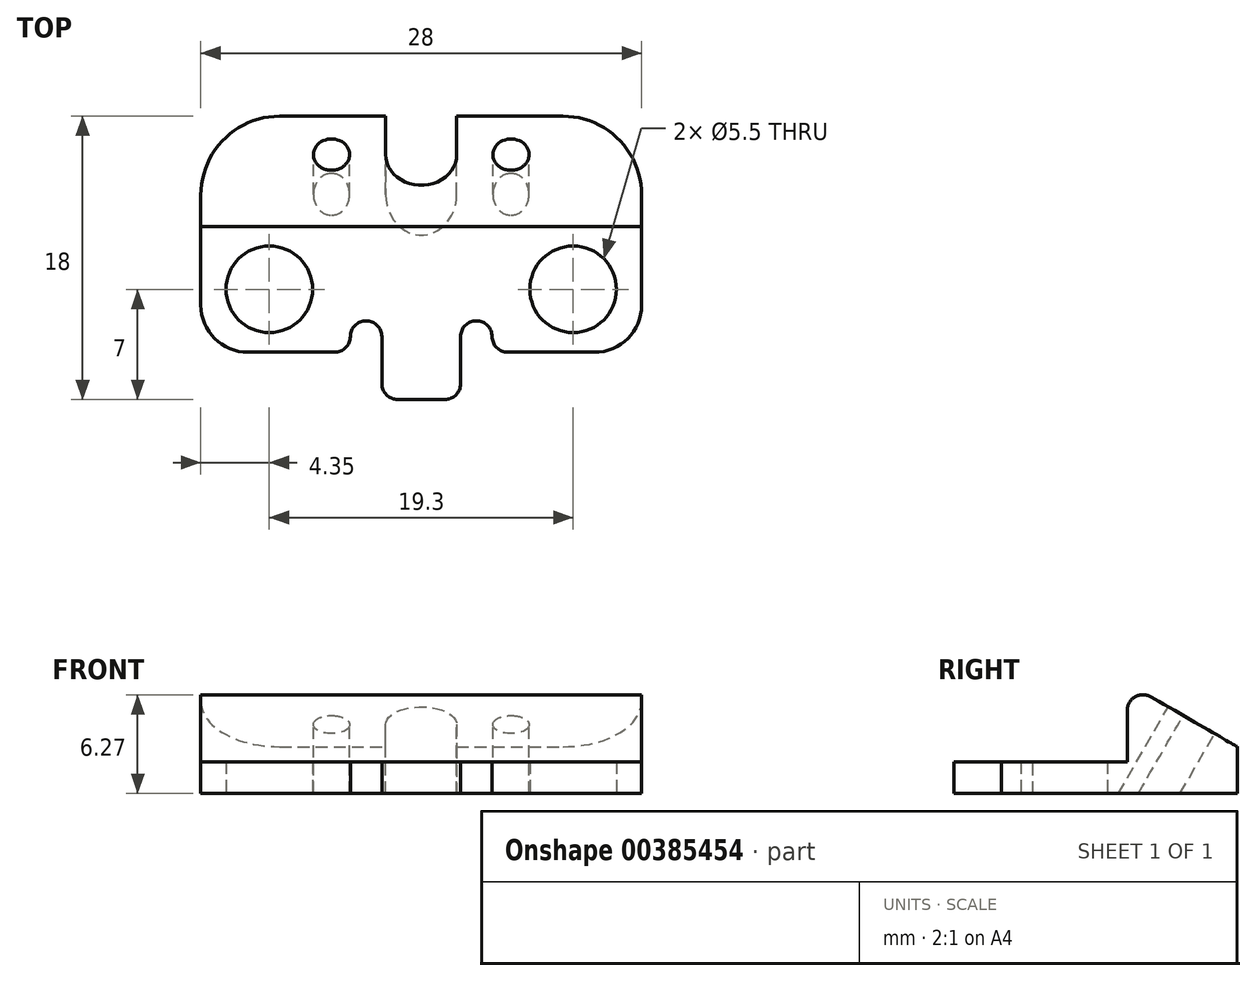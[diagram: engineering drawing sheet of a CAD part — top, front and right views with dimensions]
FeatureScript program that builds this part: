
annotation { "Feature Type Name" : "Feature", "Feature Type Description" : "" }
export const myFeature = defineFeature(function(context is Context, id is Id, definition is map)
    precondition{}
    {
        {
            var Q0;
            Q0=qCreatedBy(makeId("Top.planeOp"),FACE);
            var sketch = newSketch(context, id + "F0", { "sketchPlane" : qUnion([Q0])});
            skLineSegment(sketch, "E0", {"start": v(-14, -10) * mm, "end": v(-14, -2) * mm});
            skLineSegment(sketch, "E1", {"start": v(-14, -2) * mm, "end": v(14, -2) * mm});
            skLineSegment(sketch, "E2", {"start": v(14, -2) * mm, "end": v(14, -10) * mm});
            skLineSegment(sketch, "E3", {"start": v(14, -10) * mm, "end": v(-14, -10) * mm});
            skPoint(sketch, "E4", {"position": v(-9.65, -6) * mm});
            skPoint(sketch, "E4.positionSnap0", {"position": v(-14, -6) * mm});
            skPoint(sketch, "E5", {"position": v(9.65, -6) * mm});
            skPoint(sketch, "E5.positionSnap0", {"position": v(14, -6) * mm});
            skLineSegment(sketch, "E6", {"start": v(-14, -2) * mm, "end": v(-14, 5) * mm});
            skLineSegment(sketch, "E7", {"start": v(-14, 5) * mm, "end": v(14, 5) * mm});
            skLineSegment(sketch, "E8", {"start": v(14, 5) * mm, "end": v(14, -2) * mm});
            skPoint(sketch, "E9", {"position": v(0, 0) * mm});
            skPoint(sketch, "E10.positionSnap0", {"position": v(14, 1.5) * mm});
            skPoint(sketch, "E10.positionSnap1", {"position": v(0, 5) * mm});
            skLineSegment(sketch, "E11", {"start": v(2.5, -10) * mm, "end": v(2.5, -13) * mm});
            skLineSegment(sketch, "E12", {"start": v(2.5, -13) * mm, "end": v(-2.5, -13) * mm});
            skLineSegment(sketch, "E13", {"start": v(-2.5, -13) * mm, "end": v(-2.5, -10) * mm});
            skLineSegment(sketch, "E14", {"start": v(2.5, -10) * mm, "end": v(2.5, -8) * mm});
            skLineSegment(sketch, "E15", {"start": v(2.5, -8) * mm, "end": v(4.5, -8) * mm});
            skLineSegment(sketch, "E16", {"start": v(4.5, -8) * mm, "end": v(4.5, -10) * mm});
            skLineSegment(sketch, "E17", {"start": v(-2.5, -10) * mm, "end": v(-2.5, -8) * mm});
            skLineSegment(sketch, "E18", {"start": v(-2.5, -8) * mm, "end": v(-4.5, -8) * mm});
            skLineSegment(sketch, "E19", {"start": v(-4.5, -8) * mm, "end": v(-4.5, -10) * mm});
            skSolve(sketch);
        }
        {
            var Q0;
            Q0=makeQuery(id+"F0.imprint","IMPRINT",FACE,{"disambiguationData":[TD([[makeQuery(id+"F0.imprint","IMPRINT",EDGE,{"derivedFrom":sQuery(id+"F0.wireOp",EDGE,"E0")}),-1.0]])]});
            var Q1;
            {var subQ0=sQuery(id+"F0.wireOp",EDGE,"E11");Q1=makeQuery(id+"F0.imprint","IMPRINT",FACE,{"disambiguationData":[TD([[makeQuery(id+"F0.imprint","IMPRINT",EDGE,{"derivedFrom":subQ0}),-1.0]])]});}
            extrude(context, id + "F1", {"entities" : qUnion([Q0, Q1]), "depth" : 2 * mm, "offsetDistance" : 25 * mm});
        }
        {
            var Q0;
            Q0=makeQuery(id+"F0.imprint","IMPRINT",FACE,{"disambiguationData":[TD([[makeQuery(id+"F0.imprint","IMPRINT",EDGE,{"derivedFrom":sQuery(id+"F0.wireOp",EDGE,"E1")}),1.0]])]});
            extrude(context, id + "F2", {"entities" : qUnion([Q0]), "operationType" : NewBodyOperationType.ADD, "depth" : 7 * mm, "offsetDistance" : 25 * mm});
        }
        {
            var Q0;
            Q0=sQuery(id+"F0.wireOp",VERTEX,"E4");
            var Q1;
            Q1=sQuery(id+"F0.wireOp",VERTEX,"E5");
            var Q2;
            Q2=makeQuery(id+"F1.opExtrude","SWEPT_BODY",BODY,{"disambiguationData":[OSD([sQuery(id+"F0.wireOp",EDGE,"E0"),sQuery(id+"F0.wireOp",EDGE,"E1"),sQuery(id+"F0.wireOp",EDGE,"E2"),sQuery(id+"F0.wireOp",EDGE,"E3")])]});
            hole(context, id + "F3", {"style" : HoleStyle.SIMPLE, "endStyle" : HoleEndStyle.THROUGH, "oppositeDirection" : true, "holeDiameter" : 5.5 * mm, "isTappedThrough" : true, "tappedDepth" : 12 * mm, "tapClearance" : 3, "locations" : qUnion([Q0, Q1]), "scope" : qUnion([Q2])});
        }
        {
            var Q0;
            Q0=makeQuery(id+"F2.boolean.opBoolean","MERGE",FACE,{"derivedFrom":[makeQuery(id+"F1.opExtrude","SWEPT_FACE",FACE,{"disambiguationData":[OSD([sQuery(id+"F0.wireOp",EDGE,"E2")])]}),makeQuery(id+"F2.opExtrude","SWEPT_FACE",FACE,{"disambiguationData":[OSD([sQuery(id+"F0.wireOp",EDGE,"E8")])]})]});
            var sketch = newSketch(context, id + "F4", { "sketchPlane" : qUnion([Q0])});
            skLineSegment(sketch, "E20", {"start": v(-2, 7) * mm, "end": v(5, 2.96) * mm});
            skSolve(sketch);
        }
        {
            var Q0;
            {var subQ0=sQuery(id+"F4.wireOp",EDGE,"E20");Q0=makeQuery(id+"F4.imprint","IMPRINT",FACE,{"disambiguationData":[TD([[makeQuery(id+"F4.imprint","IMPRINT",EDGE,{"derivedFrom":subQ0}),1.0]])]});}
            extrude(context, id + "F5", {"entities" : qUnion([Q0]), "operationType" : NewBodyOperationType.REMOVE, "endBound" : BoundingType.THROUGH_ALL, "oppositeDirection" : true, "depth" : 25 * mm});
        }
        {
            var Q0;
            Q0=makeQuery(id+"F1.opExtrude","SWEPT_EDGE",EDGE,{"disambiguationData":[OSD([sQuery(id+"F0.wireOp",EDGE,"E0"),sQuery(id+"F0.wireOp",EDGE,"E3")])]});
            var Q1;
            Q1=makeQuery(id+"F1.opExtrude","SWEPT_EDGE",EDGE,{"disambiguationData":[OSD([sQuery(id+"F0.wireOp",EDGE,"E2"),sQuery(id+"F0.wireOp",EDGE,"E3")])]});
            fillet(context, id + "F6", {"entities" : qUnion([Q0, Q1]), "radius" : 3 * mm, "tangentPropagation" : true, "allowEdgeOverflow" : false});
        }
        {
            var Q0;
            Q0=makeQuery(id+"F2.opExtrude","SWEPT_EDGE",EDGE,{"disambiguationData":[OSD([sQuery(id+"F0.wireOp",EDGE,"E7"),sQuery(id+"F0.wireOp",EDGE,"E8")])]});
            var Q1;
            Q1=makeQuery(id+"F2.opExtrude","SWEPT_EDGE",EDGE,{"disambiguationData":[OSD([sQuery(id+"F0.wireOp",EDGE,"E6"),sQuery(id+"F0.wireOp",EDGE,"E7")])]});
            fillet(context, id + "F7", {"entities" : qUnion([Q0, Q1]), "radius" : 5 * mm, "tangentPropagation" : true, "allowEdgeOverflow" : false});
        }
        {
            var Q0;
            Q0=makeQuery(id+"F2.opExtrude","SWEPT_EDGE",EDGE,{"disambiguationData":[OSD([sQuery(id+"F0.wireOp",EDGE,"E7"),sQuery(id+"F0.wireOp",EDGE,"al64L23N-QREo-ytZC-Y57I-qEylZoFodaZA")])]});
            var Q1;
            Q1=makeQuery(id+"F2.opExtrude","SWEPT_EDGE",EDGE,{"disambiguationData":[OSD([sQuery(id+"F0.wireOp",EDGE,"E7"),sQuery(id+"F0.wireOp",EDGE,"A9lWMWF5-5aLG-td5A-o3ft-i0FPsXMzaifF")])]});
            var Q2;
            Q2=makeQuery(id+"F2.opExtrude","CAP_EDGE",EDGE,{"disambiguationData":[OSD([sQuery(id+"F0.wireOp",EDGE,"E1")])],"isStart":false});
            var Q3;
            Q3=makeQuery(id+"F1.opExtrude","SWEPT_EDGE",EDGE,{"disambiguationData":[OSD([sQuery(id+"F0.wireOp",EDGE,"E18"),sQuery(id+"F0.wireOp",EDGE,"E19")])]});
            var Q4;
            Q4=makeQuery(id+"F1.opExtrude","SWEPT_EDGE",EDGE,{"disambiguationData":[OSD([sQuery(id+"F0.wireOp",EDGE,"E17"),sQuery(id+"F0.wireOp",EDGE,"E18")])]});
            var Q5;
            Q5=makeQuery(id+"F1.opExtrude","SWEPT_EDGE",EDGE,{"disambiguationData":[OSD([sQuery(id+"F0.wireOp",EDGE,"E14"),sQuery(id+"F0.wireOp",EDGE,"E15")])]});
            var Q6;
            Q6=makeQuery(id+"F1.opExtrude","SWEPT_EDGE",EDGE,{"disambiguationData":[OSD([sQuery(id+"F0.wireOp",EDGE,"E15"),sQuery(id+"F0.wireOp",EDGE,"E16")])]});
            var Q7;
            Q7=makeQuery(id+"F1.opExtrude","SWEPT_EDGE",EDGE,{"disambiguationData":[OSD([sQuery(id+"F0.wireOp",EDGE,"E3"),sQuery(id+"F0.wireOp",EDGE,"E16")])]});
            var Q8;
            Q8=makeQuery(id+"F1.opExtrude","SWEPT_EDGE",EDGE,{"disambiguationData":[OSD([sQuery(id+"F0.wireOp",EDGE,"E3"),sQuery(id+"F0.wireOp",EDGE,"E19")])]});
            var Q9;
            Q9=makeQuery(id+"F1.opExtrude","SWEPT_EDGE",EDGE,{"disambiguationData":[OSD([sQuery(id+"F0.wireOp",EDGE,"E12"),sQuery(id+"F0.wireOp",EDGE,"E13")])]});
            var Q10;
            Q10=makeQuery(id+"F1.opExtrude","SWEPT_EDGE",EDGE,{"disambiguationData":[OSD([sQuery(id+"F0.wireOp",EDGE,"E11"),sQuery(id+"F0.wireOp",EDGE,"E12")])]});
            fillet(context, id + "F8", {"entities" : qUnion([Q0, Q1, Q2, Q3, Q4, Q5, Q6, Q7, Q8, Q9, Q10]), "radius" : 1 * mm, "tangentPropagation" : true, "allowEdgeOverflow" : false});
        }
        {
            var Q0;
            Q0=makeQuery(id+"F5.boolean.opBoolean","COPY",FACE,{"derivedFrom":makeQuery(id+"F5.opExtrude","SWEPT_FACE",FACE,{"disambiguationData":[OSD([sQuery(id+"F4.wireOp",EDGE,"E20")])]})});
            var sketch = newSketch(context, id + "F9", { "sketchPlane" : qUnion([Q0])});
            skLineSegment(sketch, "E21", {"start": v(-2.25, 2.85) * mm, "end": v(-2.25, 0.03) * mm});
            skLineSegment(sketch, "E22", {"start": v(2.25, 0.03) * mm, "end": v(2.25, 2.85) * mm});
            skArc(sketch, "E23", {"start": v(-2.25, 0.03) * mm, "mid": v(0, -2.22) * mm, "end": v(2.25, 0.03) * mm});
            skPoint(sketch, "E24", {"position": v(-5.7, 0.03) * mm});
            skPoint(sketch, "E25", {"position": v(5.7, 0.03) * mm});
            skLineSegment(sketch, "E26", {"start": v(2.25, 2.85) * mm, "end": v(2.25, 5.99) * mm});
            skLineSegment(sketch, "E27", {"start": v(2.25, 5.99) * mm, "end": v(-2.25, 5.99) * mm});
            skLineSegment(sketch, "E28", {"start": v(-2.25, 5.99) * mm, "end": v(-2.25, 2.85) * mm});
            skSolve(sketch);
        }
        {
            var Q0;
            {var subQ0=sQuery(id+"F9.wireOp",EDGE,"E21");Q0=makeQuery(id+"F9.imprint","IMPRINT",FACE,{"disambiguationData":[TD([[makeQuery(id+"F9.imprint","IMPRINT",EDGE,{"derivedFrom":subQ0}),1.0]])]});}
            var Q1;
            {var subQ0=sQuery(id+"F9.wireOp",EDGE,"E26");Q1=makeQuery(id+"F9.imprint","IMPRINT",FACE,{"disambiguationData":[TD([[makeQuery(id+"F9.imprint","IMPRINT",EDGE,{"derivedFrom":subQ0}),1.0]])]});}
            extrude(context, id + "F10", {"entities" : qUnion([Q0, Q1]), "operationType" : NewBodyOperationType.REMOVE, "oppositeDirection" : true, "depth" : 25 * mm});
        }
        {
            var Q0;
            Q0=sQuery(id+"F9.wireOp",VERTEX,"E25");
            var Q1;
            Q1=sQuery(id+"F9.wireOp",VERTEX,"E24");
            var Q2;
            Q2=makeQuery(id+"F1.opExtrude","SWEPT_BODY",BODY,{"disambiguationData":[OSD([sQuery(id+"F0.wireOp",EDGE,"E0"),sQuery(id+"F0.wireOp",EDGE,"E1"),sQuery(id+"F0.wireOp",EDGE,"E2"),sQuery(id+"F0.wireOp",EDGE,"E3")])]});
            hole(context, id + "F11", {"style" : HoleStyle.SIMPLE, "endStyle" : HoleEndStyle.THROUGH, "holeDiameter" : 2.3 * mm, "isTappedThrough" : true, "tappedDepth" : 12 * mm, "tapClearance" : 3, "locations" : qUnion([Q0, Q1]), "scope" : qUnion([Q2])});
        }
    });
